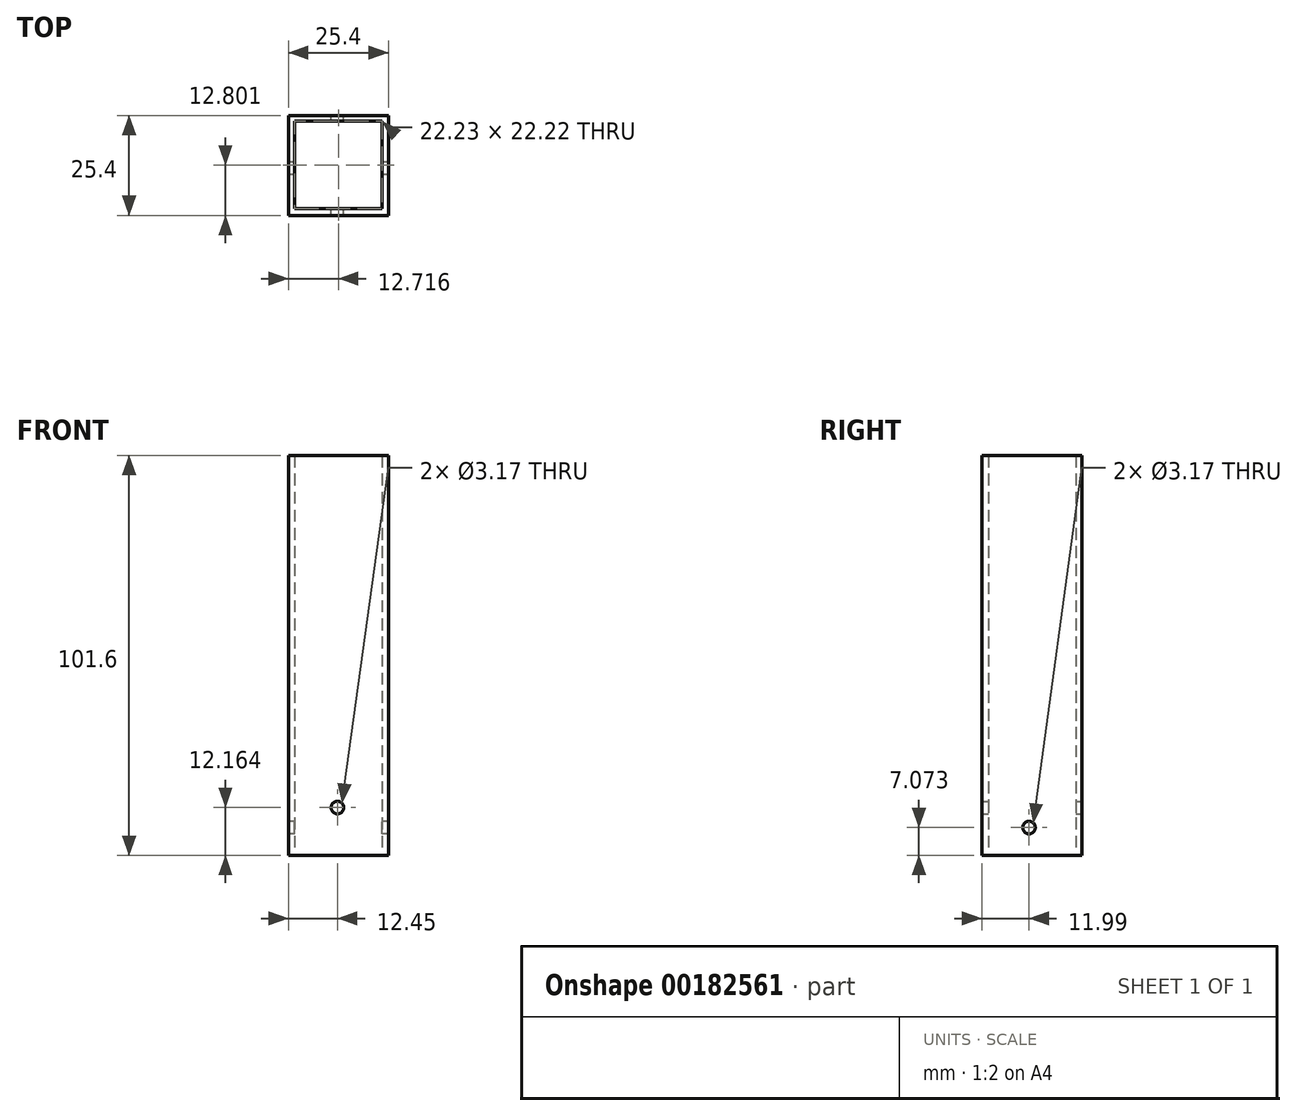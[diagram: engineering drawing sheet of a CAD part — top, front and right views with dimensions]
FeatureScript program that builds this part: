
annotation { "Feature Type Name" : "Feature", "Feature Type Description" : "" }
export const myFeature = defineFeature(function(context is Context, id is Id, definition is map)
    precondition{}
    {
        {
            var Q0;
            Q0=qCreatedBy(makeId("Top.planeOp"),FACE);
            var sketch = newSketch(context, id + "F0", { "sketchPlane" : qUnion([Q0])});
            skLineSegment(sketch, "E0.bottom", {"start": v(8.37, -14.95) * mm, "end": v(33.77, -14.95) * mm});
            skLineSegment(sketch, "E0.top", {"start": v(8.37, -40.35) * mm, "end": v(33.77, -40.35) * mm});
            skLineSegment(sketch, "E0.left", {"start": v(8.37, -14.95) * mm, "end": v(8.37, -40.35) * mm});
            skLineSegment(sketch, "E0.right", {"start": v(33.77, -14.95) * mm, "end": v(33.77, -40.35) * mm});
            skSolve(sketch);
        }
        {
            var Q0;
            Q0=makeQuery(id+"F0.imprint","IMPRINT",FACE,{"disambiguationData":[TD([[makeQuery(id+"F0.imprint","IMPRINT",EDGE,{"derivedFrom":sQuery(id+"F0.wireOp",EDGE,"E0.bottom")}),-1.0]])]});
            var sketch = newSketch(context, id + "F1", { "sketchPlane" : qUnion([Q0])});
            skLineSegment(sketch, "E1.bottom", {"start": v(9.97, -16.44) * mm, "end": v(32.2, -16.44) * mm});
            skLineSegment(sketch, "E1.top", {"start": v(9.97, -38.66) * mm, "end": v(32.2, -38.66) * mm});
            skLineSegment(sketch, "E1.left", {"start": v(9.97, -16.44) * mm, "end": v(9.97, -38.66) * mm});
            skLineSegment(sketch, "E1.right", {"start": v(32.2, -16.44) * mm, "end": v(32.2, -38.66) * mm});
            skSolve(sketch);
        }
        {
            var Q0;
            Q0=makeQuery(id+"F1.imprint","IMPRINT",FACE,{"disambiguationData":[TD([[makeQuery(id+"F1.imprint","IMPRINT",EDGE,{"derivedFrom":sQuery(id+"F1.wireOp",EDGE,"E1.bottom")}),1.0]])]});
            extrude(context, id + "F2", {"entities" : qUnion([Q0]), "depth" : 101.6 * mm});
        }
        {
            var Q0;
            Q0=makeQuery(id+"F2.opExtrude","SWEPT_FACE",FACE,{"disambiguationData":[OSD([sQuery(id+"F0.wireOp",EDGE,"E0.bottom")])]});
            var sketch = newSketch(context, id + "F3", { "sketchPlane" : qUnion([Q0])});
            skCircle(sketch, "E2", {"center": v(-20.82, 12.16) * mm, "radius": 1.59 * mm});
            skSolve(sketch);
        }
        {
            var Q0;
            Q0=sQuery(id+"F3.wireOp",VERTEX,"E2.center");
            var Q1;
            Q1=makeQuery(id+"F2.opExtrude","SWEPT_BODY",BODY,{"disambiguationData":[OSD([sQuery(id+"F0.wireOp",EDGE,"E0.bottom"),sQuery(id+"F0.wireOp",EDGE,"E0.top"),sQuery(id+"F0.wireOp",EDGE,"E0.left"),sQuery(id+"F0.wireOp",EDGE,"E0.right"),sQuery(id+"F1.wireOp",EDGE,"E1.bottom"),sQuery(id+"F1.wireOp",EDGE,"E1.top"),sQuery(id+"F1.wireOp",EDGE,"E1.left"),sQuery(id+"F1.wireOp",EDGE,"E1.right")])]});
            hole(context, id + "F4", {"style" : HoleStyle.SIMPLE, "endStyle" : HoleEndStyle.THROUGH, "holeDiameter" : 3.17 * mm, "startFromSketch" : true, "locations" : qUnion([Q0]), "scope" : qUnion([Q1]), "isTappedThrough" : true});
        }
        {
            var Q0;
            Q0=makeQuery(id+"F2.opExtrude","SWEPT_FACE",FACE,{"disambiguationData":[OSD([sQuery(id+"F0.wireOp",EDGE,"E0.left")])]});
            var sketch = newSketch(context, id + "F5", { "sketchPlane" : qUnion([Q0])});
            skCircle(sketch, "E3", {"center": v(28.36, 7.07) * mm, "radius": 1.59 * mm});
            skSolve(sketch);
        }
        {
            var Q0;
            Q0=sQuery(id+"F5.wireOp",VERTEX,"E3.center");
            var Q1;
            Q1=makeQuery(id+"F2.opExtrude","SWEPT_BODY",BODY,{"disambiguationData":[OSD([sQuery(id+"F0.wireOp",EDGE,"E0.bottom"),sQuery(id+"F0.wireOp",EDGE,"E0.top"),sQuery(id+"F0.wireOp",EDGE,"E0.left"),sQuery(id+"F0.wireOp",EDGE,"E0.right"),sQuery(id+"F1.wireOp",EDGE,"E1.bottom"),sQuery(id+"F1.wireOp",EDGE,"E1.top"),sQuery(id+"F1.wireOp",EDGE,"E1.left"),sQuery(id+"F1.wireOp",EDGE,"E1.right")])]});
            hole(context, id + "F6", {"style" : HoleStyle.SIMPLE, "endStyle" : HoleEndStyle.THROUGH, "holeDiameter" : 3.17 * mm, "startFromSketch" : true, "locations" : qUnion([Q0]), "scope" : qUnion([Q1]), "isTappedThrough" : true});
        }
    });
